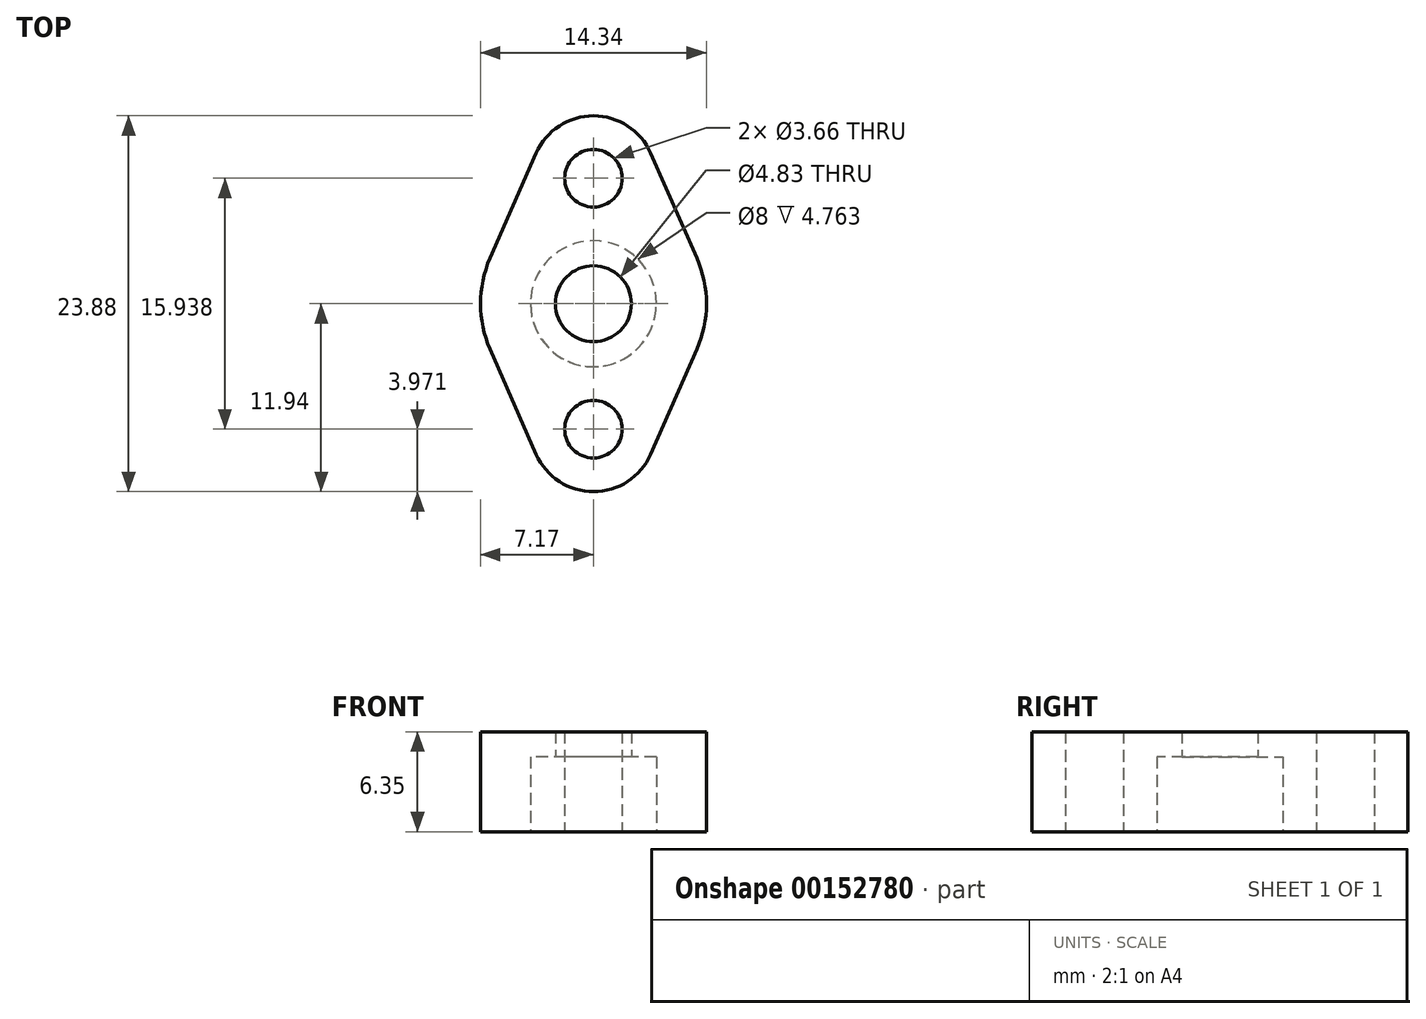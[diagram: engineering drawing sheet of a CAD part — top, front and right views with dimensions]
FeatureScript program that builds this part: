
annotation { "Feature Type Name" : "Feature", "Feature Type Description" : "" }
export const myFeature = defineFeature(function(context is Context, id is Id, definition is map)
    precondition{}
    {
        {
            var Q0;
            Q0=qCreatedBy(makeId("Top.planeOp"),FACE);
            var sketch = newSketch(context, id + "F0", { "sketchPlane" : qUnion([Q0])});
            skCircle(sketch, "E0", {"center": v(0, 0) * mm, "radius": 4 * mm, "construction": true});
            skLineSegment(sketch, "E1", {"start": v(0, 7.97) * mm, "end": v(0, -7.97) * mm, "construction": true});
            skArc(sketch, "E2", {"start": v(-3.63, 9.57) * mm, "mid": v(0, 4) * mm, "end": v(3.63, 9.57) * mm, "construction": true});
            skArc(sketch, "E3", {"start": v(3.63, 9.57) * mm, "mid": v(0, 11.94) * mm, "end": v(-3.63, 9.57) * mm});
            skArc(sketch, "E4", {"start": v(-3.63, -9.57) * mm, "mid": v(0, -11.94) * mm, "end": v(3.63, -9.57) * mm});
            skArc(sketch, "E5", {"start": v(6.57, -2.89) * mm, "mid": v(7.18, 0) * mm, "end": v(6.57, 2.89) * mm});
            skArc(sketch, "E6", {"start": v(-6.57, 2.89) * mm, "mid": v(-7.18, 0) * mm, "end": v(-6.57, -2.89) * mm});
            skLineSegment(sketch, "E7", {"start": v(3.63, 9.57) * mm, "end": v(6.57, 2.89) * mm});
            skLineSegment(sketch, "E8", {"start": v(6.57, -2.89) * mm, "end": v(3.63, -9.57) * mm});
            skLineSegment(sketch, "E9", {"start": v(-3.63, 9.57) * mm, "end": v(-6.57, 2.89) * mm});
            skLineSegment(sketch, "E10", {"start": v(-3.63, -9.57) * mm, "end": v(-6.57, -2.89) * mm});
            skCircle(sketch, "E11", {"center": v(0, 7.97) * mm, "radius": 1.83 * mm});
            skCircle(sketch, "E12", {"center": v(0, -7.97) * mm, "radius": 1.83 * mm});
            skCircle(sketch, "E13", {"center": v(0, 0) * mm, "radius": 2.41 * mm});
            skSolve(sketch);
        }
        {
            var Q0;
            Q0 = qSketchRegion(id + "F0", true);
            extrude(context, id + "F1", {"entities" : qUnion([Q0]), "depth" : 6.35 * mm});
        }
        {
            var Q0;
            Q0=makeQuery(id+"F1.opExtrude","CAP_FACE",FACE,{"disambiguationData":[OSD([sQuery(id+"F0.wireOp",EDGE,"E3"),sQuery(id+"F0.wireOp",EDGE,"E4"),sQuery(id+"F0.wireOp",EDGE,"E5"),sQuery(id+"F0.wireOp",EDGE,"E6"),sQuery(id+"F0.wireOp",EDGE,"E7"),sQuery(id+"F0.wireOp",EDGE,"E8"),sQuery(id+"F0.wireOp",EDGE,"E9"),sQuery(id+"F0.wireOp",EDGE,"E10"),sQuery(id+"F0.wireOp",EDGE,"E11"),sQuery(id+"F0.wireOp",EDGE,"E12"),sQuery(id+"F0.wireOp",EDGE,"E13")])],"isStart":false});
            cPlane(context, id + "F2", {"entities" : qUnion([Q0]), "cplaneType" : CPlaneType.OFFSET, "offset" : 1.59 * mm, "oppositeDirection" : true, "width" : 152.4 * mm, "height" : 152.4 * mm});
        }
        {
            var Q0;
            Q0=makeQuery(id+"F1.opExtrude","CAP_FACE",FACE,{"disambiguationData":[OSD([sQuery(id+"F0.wireOp",EDGE,"E3"),sQuery(id+"F0.wireOp",EDGE,"E4"),sQuery(id+"F0.wireOp",EDGE,"E5"),sQuery(id+"F0.wireOp",EDGE,"E6"),sQuery(id+"F0.wireOp",EDGE,"E7"),sQuery(id+"F0.wireOp",EDGE,"E8"),sQuery(id+"F0.wireOp",EDGE,"E9"),sQuery(id+"F0.wireOp",EDGE,"E10"),sQuery(id+"F0.wireOp",EDGE,"E11"),sQuery(id+"F0.wireOp",EDGE,"E12"),sQuery(id+"F0.wireOp",EDGE,"E13")])],"isStart":true});
            var sketch = newSketch(context, id + "F3", { "sketchPlane" : qUnion([Q0])});
            skCircle(sketch, "E14", {"center": v(0, 0) * mm, "radius": 4 * mm});
            skSolve(sketch);
        }
        {
            var Q0;
            Q0 = qSketchRegion(id + "F3", true);
            var Q1;
            Q1=qCreatedBy(id+"F2.planeOp",FACE);
            extrude(context, id + "F4", {"entities" : qUnion([Q0]), "operationType" : NewBodyOperationType.REMOVE, "endBound" : BoundingType.UP_TO_SURFACE, "oppositeDirection" : true, "endBoundEntityFace" : qUnion([Q1]), "depth" : 25.4 * mm});
        }
    });
